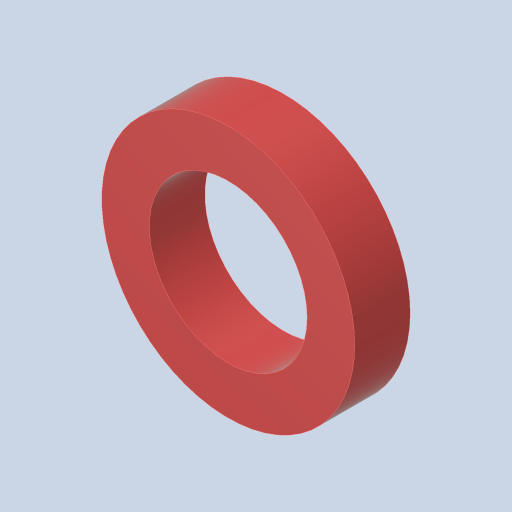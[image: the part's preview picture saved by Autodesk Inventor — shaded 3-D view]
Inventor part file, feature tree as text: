
AUTODESK INVENTOR PART (.ipt)
format: ipt  version: 2023.4 (Build 274418000, 418)  size: 111,616 bytes
history: native  units: in
note: dims shown in document units (in); Inventor stores cm internally (conversion verified against a paired STEP export)
features: extrude x1, sketch x1
ambient origin geometry x8: Origin, YZ Plane, XZ Plane, XY Plane, X Axis, Y Axis, Z Axis, Center Point
bodies: Solid1 (feature_tree)
feature tree (2):
  extrude  "Extrusion1"  Depth=0.146in
  sketch  "Sketch1"  dims[d0=0.415in d1=0.125in d2=0.146in d3=0.0in]
